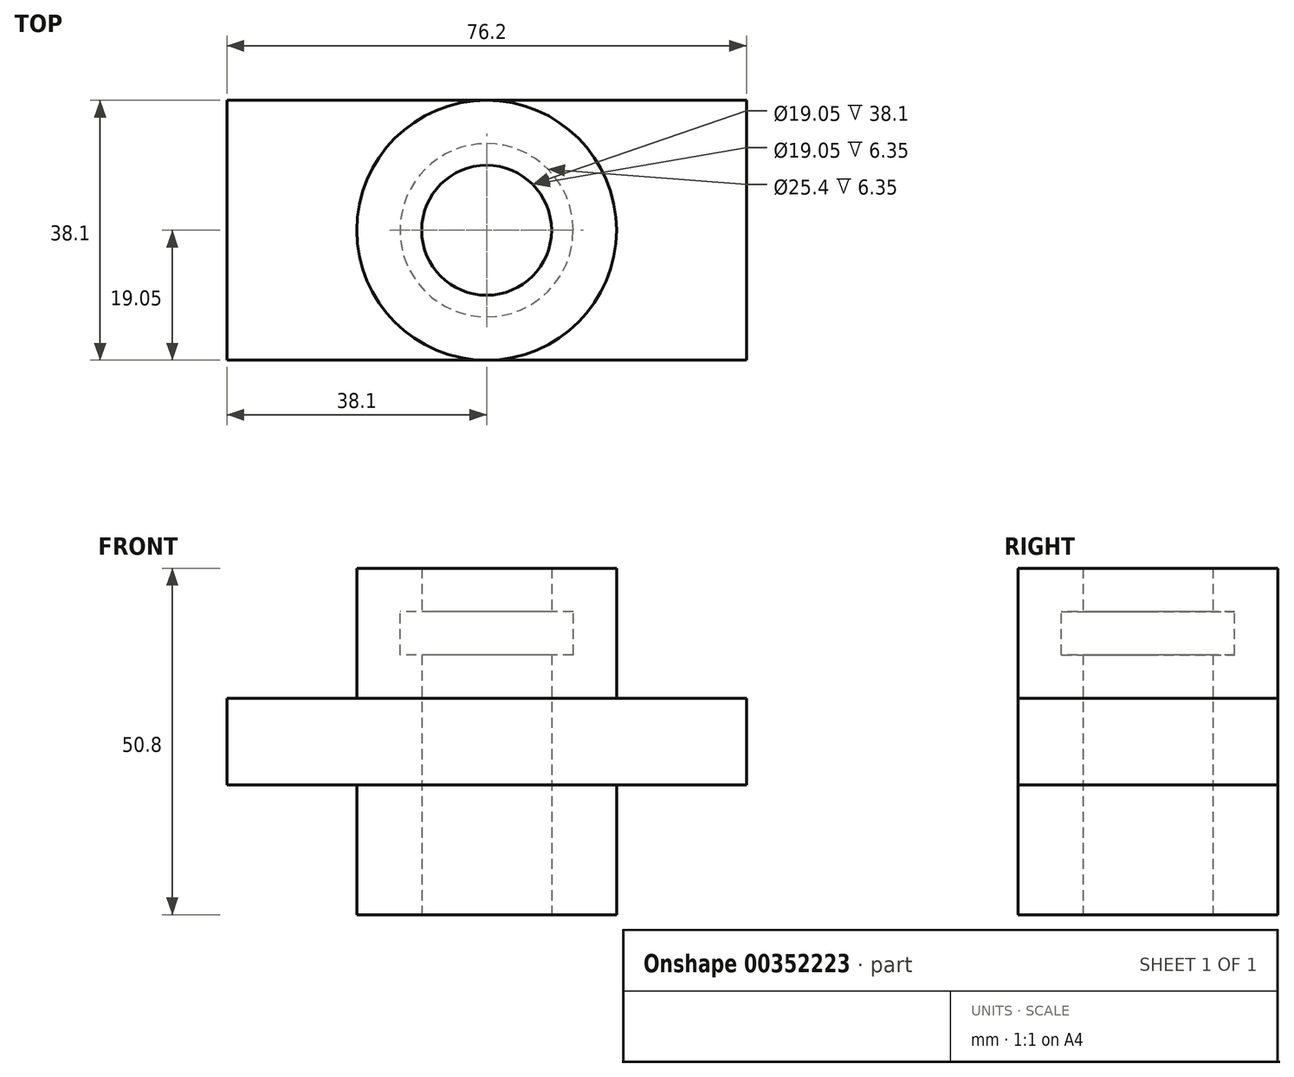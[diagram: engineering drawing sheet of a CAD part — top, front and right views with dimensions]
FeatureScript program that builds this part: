
annotation { "Feature Type Name" : "Feature", "Feature Type Description" : "" }
export const myFeature = defineFeature(function(context is Context, id is Id, definition is map)
    precondition{}
    {
        {
            var Q0;
            Q0=qCreatedBy(makeId("Top.planeOp"),FACE);
            var sketch = newSketch(context, id + "F0", { "sketchPlane" : qUnion([Q0])});
            skLineSegment(sketch, "E0", {"start": v(0, 0) * mm, "end": v(0, 38.1) * mm});
            skLineSegment(sketch, "E1", {"start": v(0, 38.1) * mm, "end": v(76.2, 38.1) * mm});
            skLineSegment(sketch, "E2", {"start": v(76.2, 38.1) * mm, "end": v(76.2, 0) * mm});
            skLineSegment(sketch, "E3", {"start": v(76.2, 0) * mm, "end": v(0, 0) * mm});
            skCircle(sketch, "E4", {"center": v(38.1, 19.05) * mm, "radius": 19.05 * mm});
            skPoint(sketch, "E4.centerSnap0", {"position": v(38.1, 0) * mm});
            skCircle(sketch, "E5", {"center": v(38.1, 19.05) * mm, "radius": 9.53 * mm});
            skSolve(sketch);
        }
        {
            var Q0;
            {var subQ0=sQuery(id+"F0.wireOp",EDGE,"E4");var subQ1=makeQuery(id+"F0.imprint","INTERSECT",VERTEX,{"derivedFrom":[sQuery(id+"F0.wireOp",EDGE,"E1"),subQ0]});Q0=makeQuery(id+"F0.imprint","IMPRINT",FACE,{"disambiguationData":[TD([[makeQuery(id+"F0.imprint","IMPRINT",EDGE,{"disambiguationData":[TD([[subQ1,-1.0]])],"derivedFrom":subQ0}),1.0]])]});}
            extrude(context, id + "F1", {"entities" : qUnion([Q0]), "endBound" : BoundingType.SYMMETRIC, "depth" : 50.8 * mm});
        }
        {
            var Q0;
            {var subQ0=sQuery(id+"F0.wireOp",EDGE,"E0");Q0=makeQuery(id+"F0.imprint","IMPRINT",FACE,{"disambiguationData":[TD([[makeQuery(id+"F0.imprint","IMPRINT",EDGE,{"derivedFrom":subQ0}),-1.0]])]});}
            var Q1;
            {var subQ0=sQuery(id+"F0.wireOp",EDGE,"E2");Q1=makeQuery(id+"F0.imprint","IMPRINT",FACE,{"disambiguationData":[TD([[makeQuery(id+"F0.imprint","IMPRINT",EDGE,{"derivedFrom":subQ0}),-1.0]])]});}
            extrude(context, id + "F2", {"entities" : qUnion([Q0, Q1]), "operationType" : NewBodyOperationType.ADD, "endBound" : BoundingType.SYMMETRIC, "depth" : 12.7 * mm});
        }
        {
            var Q0;
            Q0=makeQuery(id+"F1.opExtrude","CAP_FACE",FACE,{"disambiguationData":[OSD([sQuery(id+"F0.wireOp",EDGE,"E4"),sQuery(id+"F0.wireOp",EDGE,"E5")])],"isStart":false});
            var sketch = newSketch(context, id + "F3", { "sketchPlane" : qUnion([Q0])});
            skPoint(sketch, "E6", {"position": v(38.1, 19.05) * mm});
            skCircle(sketch, "E7", {"center": v(38.1, 19.05) * mm, "radius": 12.7 * mm});
            skSolve(sketch);
        }
        {
            var Q0;
            Q0=makeQuery(id+"F3.imprint","IMPRINT",FACE,{"disambiguationData":[TD([[makeQuery(id+"F3.imprint","IMPRINT",EDGE,{"derivedFrom":sQuery(id+"F3.wireOp",EDGE,"E7")}),1.0]])]});
            extrude(context, id + "F4", {"entities" : qUnion([Q0]), "operationType" : NewBodyOperationType.REMOVE, "oppositeDirection" : true, "depth" : 12.7 * mm, "hasSecondDirection" : true, "secondDirectionOppositeDirection" : true, "secondDirectionDepth" : 6.35 * mm});
        }
    });
